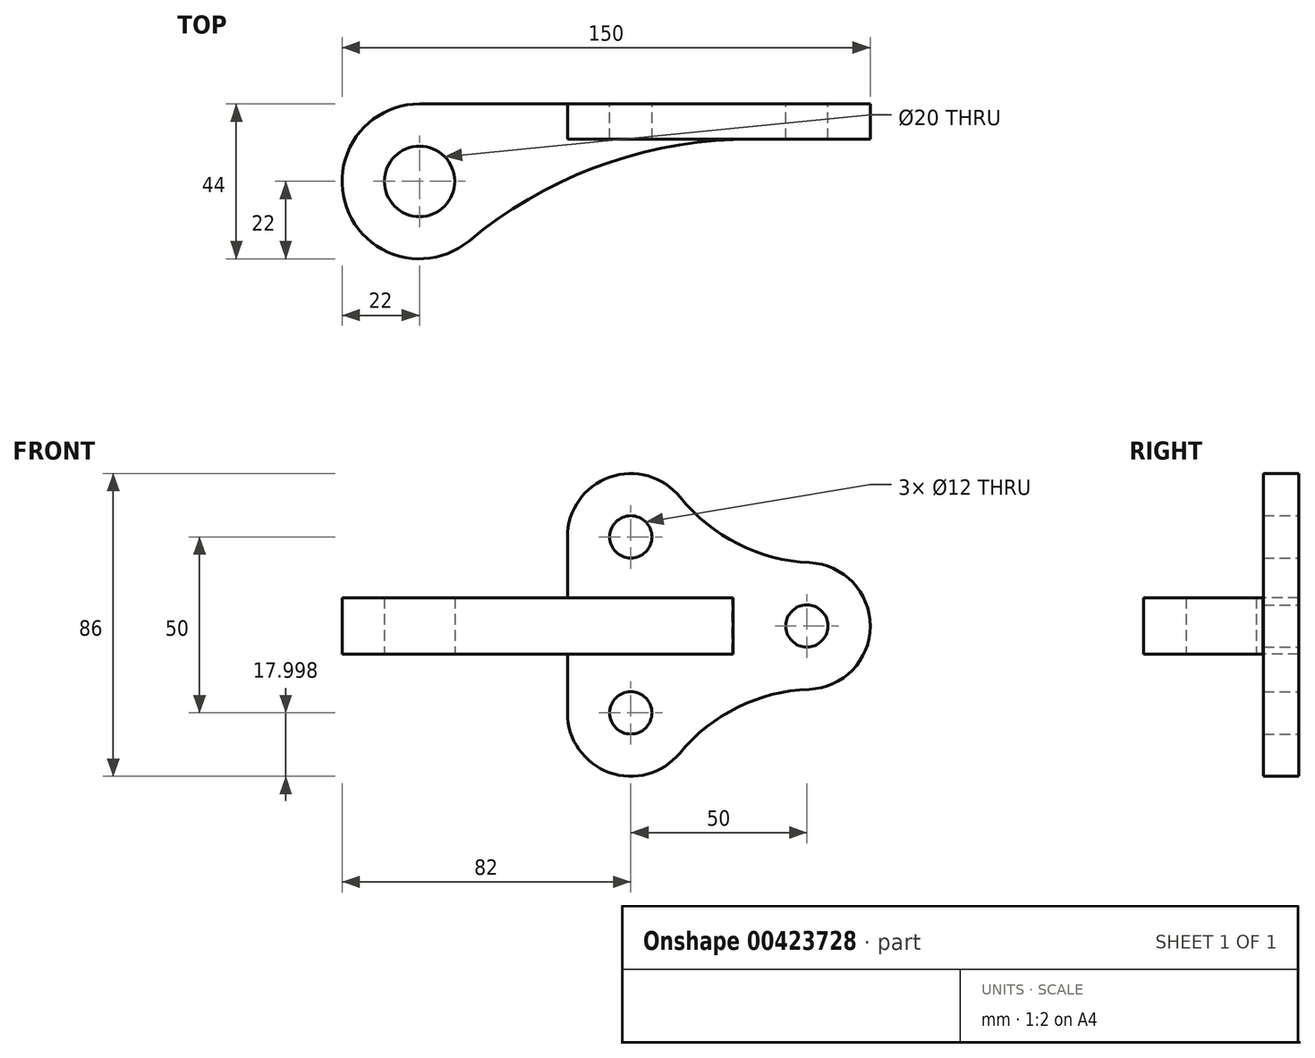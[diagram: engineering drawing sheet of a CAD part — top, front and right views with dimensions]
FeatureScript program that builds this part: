
annotation { "Feature Type Name" : "Feature", "Feature Type Description" : "" }
export const myFeature = defineFeature(function(context is Context, id is Id, definition is map)
    precondition{}
    {
        {
            var Q0;
            Q0=qCreatedBy(makeId("Front.planeOp"),FACE);
            var sketch = newSketch(context, id + "F0", { "sketchPlane" : qUnion([Q0])});
            skCircle(sketch, "E0", {"center": v(0, 25.3) * mm, "radius": 6 * mm});
            skCircle(sketch, "E1", {"center": v(0, -24.7) * mm, "radius": 6 * mm});
            skCircle(sketch, "E2", {"center": v(50, 0) * mm, "radius": 6 * mm});
            skLineSegment(sketch, "E3", {"start": v(0, 0) * mm, "end": v(50, 0) * mm});
            skLineSegment(sketch, "E4", {"start": v(0, 25.3) * mm, "end": v(0, -24.7) * mm});
            skArc(sketch, "E5", {"start": v(14.02, 36.6) * mm, "mid": v(-5.98, 42.29) * mm, "end": v(-18, 25.3) * mm});
            skArc(sketch, "E6", {"start": v(50.65, -17.99) * mm, "mid": v(68, -0.07) * mm, "end": v(50.79, 17.98) * mm});
            skArc(sketch, "E7", {"start": v(-18, -24.7) * mm, "mid": v(-6.08, -41.63) * mm, "end": v(13.89, -36.14) * mm});
            skLineSegment(sketch, "E8", {"start": v(-18, 25.3) * mm, "end": v(-18, -24.7) * mm});
            skArc(sketch, "E9", {"start": v(14.02, 36.6) * mm, "mid": v(30.4, 23.32) * mm, "end": v(50.79, 17.98) * mm});
            skArc(sketch, "E10", {"start": v(50.65, -17.99) * mm, "mid": v(30.32, -23.12) * mm, "end": v(13.89, -36.14) * mm});
            skSolve(sketch);
        }
        {
            var Q0;
            Q0=makeQuery(id+"F0.imprint","IMPRINT",FACE,{"disambiguationData":[TD([[makeQuery(id+"F0.imprint","IMPRINT",EDGE,{"derivedFrom":sQuery(id+"F0.wireOp",EDGE,"E0")}),-1.0]])]});
            extrude(context, id + "F1", {"entities" : qUnion([Q0]), "depth" : 10 * mm});
        }
        {
            var Q0;
            Q0=qCreatedBy(makeId("Top.planeOp"),FACE);
            var sketch = newSketch(context, id + "F2", { "sketchPlane" : qUnion([Q0])});
            skLineSegment(sketch, "E11", {"start": v(0, 0) * mm, "end": v(-60, 0) * mm});
            skCircle(sketch, "E12", {"center": v(-60, -22) * mm, "radius": 10 * mm});
            skArc(sketch, "E13", {"start": v(-60, 0) * mm, "mid": v(-80.69, -29.48) * mm, "end": v(-45.93, -38.91) * mm});
            skArc(sketch, "E14", {"start": v(29.11, -10.1) * mm, "mid": v(-10.79, -18.3) * mm, "end": v(-45.93, -38.91) * mm});
            skLineSegment(sketch, "E15", {"start": v(0, 0) * mm, "end": v(29.11, -10.1) * mm});
            skSolve(sketch);
        }
        {
            var Q0;
            Q0=makeQuery(id+"F2.imprint","IMPRINT",FACE,{"disambiguationData":[TD([[makeQuery(id+"F2.imprint","IMPRINT",EDGE,{"derivedFrom":sQuery(id+"F2.wireOp",EDGE,"E11")}),1.0]])]});
            extrude(context, id + "F3", {"entities" : qUnion([Q0]), "operationType" : NewBodyOperationType.ADD, "endBound" : BoundingType.SYMMETRIC, "depth" : 16 * mm});
        }
    });
